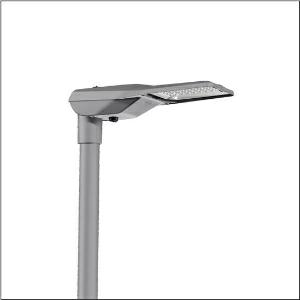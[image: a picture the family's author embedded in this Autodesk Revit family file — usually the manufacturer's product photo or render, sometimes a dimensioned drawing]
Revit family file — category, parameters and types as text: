
# Revit family: streetlight_sl_21_iq_mini___st1_0a_5xe2d41y08hb_48d2
name_source: partatom
category: Lighting Fixtures
units: mm (PartAtom-declared; Revit-internal decimal feet)

## family parameters
Cut with Voids When Loaded = No
Host = Face
Light Source = No
Part Type = Normal
Room Calculation Point = No
Round Connector Dimension = Use Diameter
Shared = No

## types (1)
- --- (1 x LED, 10080 lm, 71 W, 4000K)
    Apparent Load = 71 VA
    CIE Flux Codes = 37 72 97 100 100
    Color Rendering = 70
    Color Temperature = 4000K
    Default Elevation = 1800 mm
    Description = Streetlight SL 21 iQ mini, mast luminaire, primary light control with lens, of PMMA, primary optical cover: cover, of toughened safety glass, transparent, light distribution: ST1.0a, light emission: direct distribution, primary light characteristic: asymmetric, installation type: post-top, side-entry, LED, High Power LED, rated luminous flux: 10.080lm, luminous efficacy: 142lm/W, light colour: 740, colour temperature: 4000K, control: pre-setting: logarithmic dimming characteristic, Street-Remote, Auto-Match, Temp-Guard, Lumen-Switch, Night-Set, Smart-Wire, Light-Fading, Desk-Remote (wireless, voltage-free reading and setting of iQ features in the workshop via application-optimized NFC function/RFID function), optimised constant luminous flux control (CLO 2.0), mains connection: 220..240V, AC, 50/60Hz, start of lifetime: 71W, end of service life: 75W, reduction: 31W, luminaire housing, of diecast aluminium, powder-coated, Siteco® metallic grey (DB 702S), corrosivity category C5 mid according to DIN EN ISO 12944, please order mast flange separately, inclination adjustable: 0°, 5°, 10°, 15°, sealing non-destructively replaceable, multi-level sealing system, length: 628mm, width: 235mm, height: 110mm, mast flange for spigot size: 42mm (side-entry): 5XC10008XM4, 60/48mm (side-entry/post-top): 5XC10108XM2, 76/60mm (side-entry/post-top): 5XC10108XM1, Smart Interface below and above, protection rating (complete): IP66, insulation class (complete): insulation class II (safety insulation), certification: CE, ENEC, ENEC+, VDE, impact resistance: IK09, permissible operating ambient temperature for outdoor applications: -40..+50°C, standard-compliant lighting for roads and squares, packaging unit: 1 piece

Light Distribution: ST1.0a
    Height = 110 mm
    Lamp = 1 x LED
    Lamp Light Flux = 10080 lm
    Lamp Power = 71 W
    Lamp count = 1
    Length = 625 mm
    Luminous efficacy = 142 lm/W
    Manufacturer = Siteco
    ModVariant = No
    Model = 5XE2D41Y08HB
    Number of Poles = 1
    OnlyDefault = Yes
    Power Factor = 1
    Product Name = Streetlight SL 21 iQ mini | ST1.0a
    Product group = mast luminaire | pylon top
    ProductGroupID = 6100
    Protection Class = Protection class II
    Protection Degree = IP 66
    RLX_Detail_Level = 1
    RLX_Emergency_Light_Flux = 0 lm
    RLX_Emergency_Type = 0
    RLX_Emergency_Type_DB = No
    RlxData = <blob elided: 93957 chars, md5=b83235c1>
    Socket = socket
    Standby Power = 0 W
    System Light Flux = 10080 lm
    System Power = 71 W
    Type Comments = factory setting: luminous flux: 100 % | dim-lin: 254 | 716 mA
    Type Image = l_1003514.jpg
    URL = http://relux.com
    VarID = @adj_083567
    Voltage = 0 V
    Weight = 0.00 kg
    Width = 234 mm

## geometry (parser evidence)
native form markers: Blend x4, Sweep x11
no freeform markers — native parametric forms only
